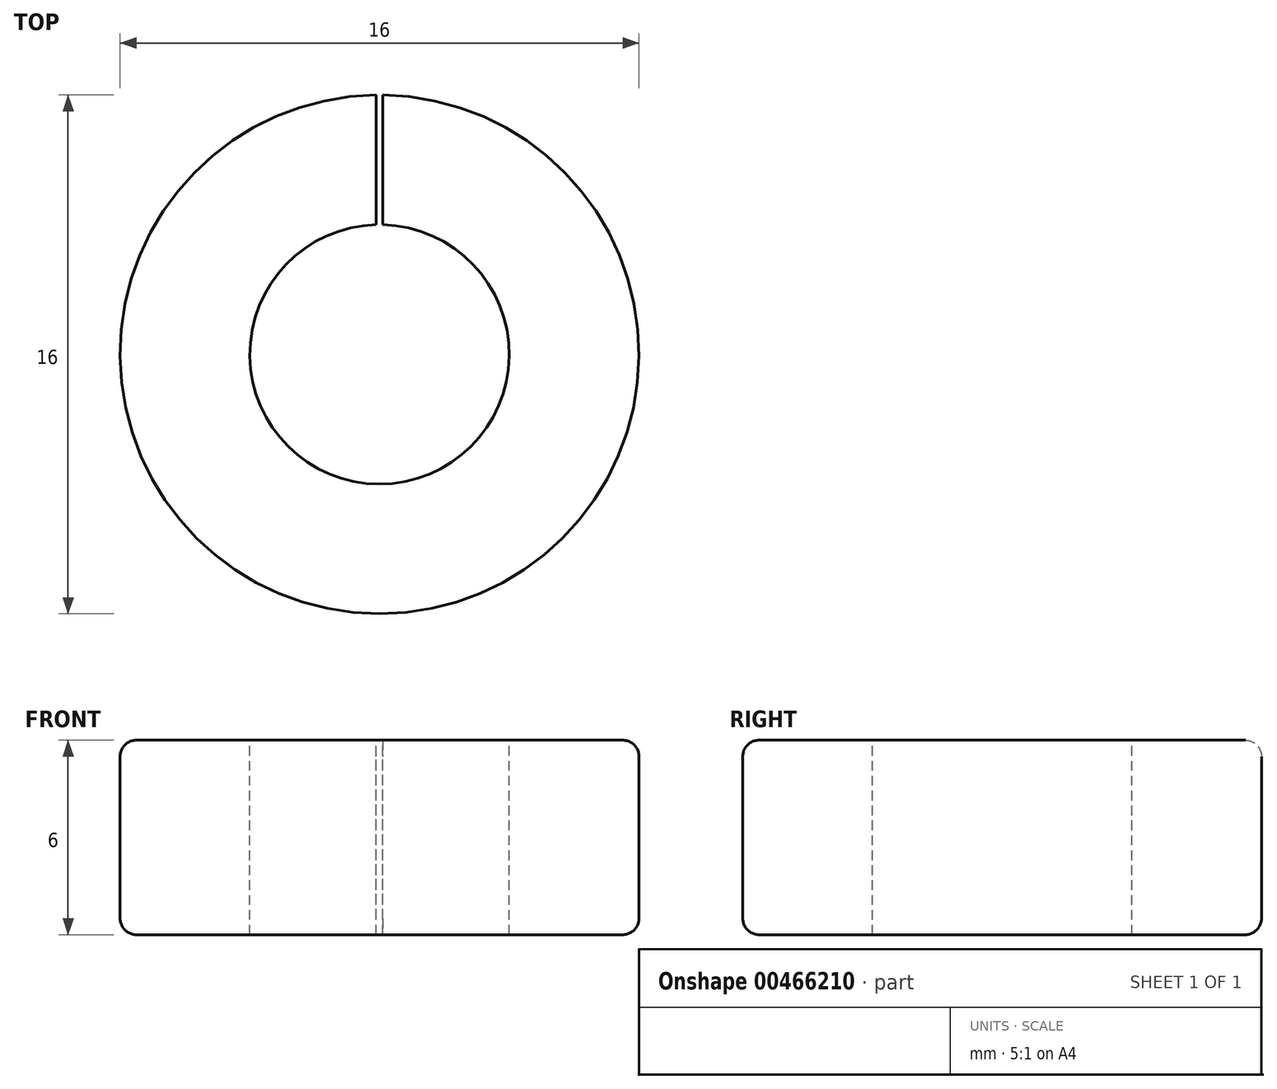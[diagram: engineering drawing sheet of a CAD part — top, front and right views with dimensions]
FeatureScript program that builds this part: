
annotation { "Feature Type Name" : "Feature", "Feature Type Description" : "" }
export const myFeature = defineFeature(function(context is Context, id is Id, definition is map)
    precondition{}
    {
        {
            var Q0;
            Q0=qCreatedBy(makeId("Top.planeOp"),FACE);
            var sketch = newSketch(context, id + "F0", { "sketchPlane" : qUnion([Q0])});
            skArc(sketch, "E0", {"start": v(-0.1, 8) * mm, "mid": v(0, -8) * mm, "end": v(0.1, 8) * mm});
            skArc(sketch, "E1", {"start": v(-0.1, 4) * mm, "mid": v(0, -4) * mm, "end": v(0.1, 4) * mm});
            skLineSegment(sketch, "E2", {"start": v(0.1, 4) * mm, "end": v(0.1, 8) * mm});
            skLineSegment(sketch, "E3.MirrorCS", {"start": v(-0.1, 4) * mm, "end": v(-0.1, 8) * mm});
            skSolve(sketch);
        }
        {
            var Q0;
            Q0=makeQuery(id+"F0.imprint","IMPRINT",FACE,{"disambiguationData":[TD([[makeQuery(id+"F0.imprint","IMPRINT",EDGE,{"derivedFrom":sQuery(id+"F0.wireOp",EDGE,"E0")}),1.0]])]});
            extrude(context, id + "F1", {"entities" : qUnion([Q0]), "oppositeDirection" : true, "depth" : 6 * mm});
        }
        {
            var Q0;
            Q0=makeQuery(id+"F1.opExtrude","CAP_EDGE",EDGE,{"disambiguationData":[OSD([sQuery(id+"F0.wireOp",EDGE,"E0")])],"isStart":true});
            var Q1;
            Q1=makeQuery(id+"F1.opExtrude","CAP_EDGE",EDGE,{"disambiguationData":[OSD([sQuery(id+"F0.wireOp",EDGE,"E0")])],"isStart":false});
            fillet(context, id + "F2", {"entities" : qUnion([Q0, Q1]), "radius" : .5 * mm, "tangentPropagation" : true, "allowEdgeOverflow" : false});
        }
    });
